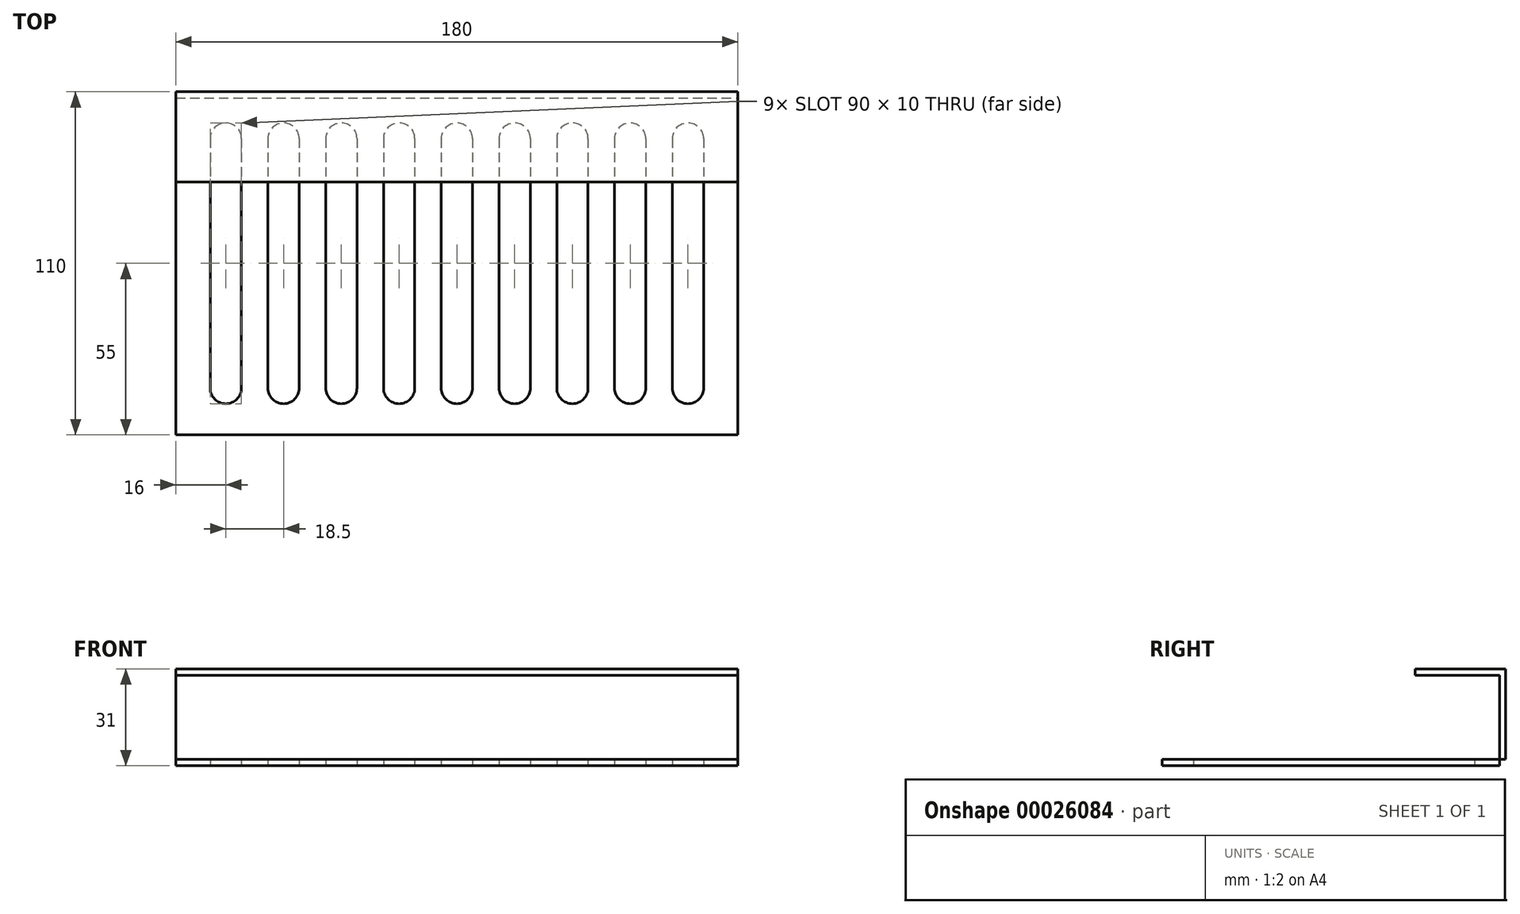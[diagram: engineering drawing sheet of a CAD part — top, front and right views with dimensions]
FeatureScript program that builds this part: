
annotation { "Feature Type Name" : "Feature", "Feature Type Description" : "" }
export const myFeature = defineFeature(function(context is Context, id is Id, definition is map)
    precondition{}
    {
        {
            var Q0;
            Q0=qCreatedBy(makeId("Top.planeOp"),FACE);
            var sketch = newSketch(context, id + "F0", { "sketchPlane" : qUnion([Q0])});
            skLineSegment(sketch, "E0.bottom", {"start": v(0, 0) * mm, "end": v(180, 0) * mm});
            skLineSegment(sketch, "E0.top", {"start": v(0, -108) * mm, "end": v(180, -108) * mm});
            skLineSegment(sketch, "E0.left", {"start": v(0, 0) * mm, "end": v(0, -108) * mm});
            skLineSegment(sketch, "E0.right", {"start": v(180, 0) * mm, "end": v(180, -108) * mm});
            skSolve(sketch);
        }
        {
            var Q0;
            Q0=makeQuery(id+"F0.imprint","IMPRINT",FACE,{"disambiguationData":[TD([[makeQuery(id+"F0.imprint","IMPRINT",EDGE,{"derivedFrom":sQuery(id+"F0.wireOp",EDGE,"E0.bottom")}),-1.0]])]});
            extrude(context, id + "F1", {"entities" : qUnion([Q0]), "depth" : 2 * mm});
        }
        {
            var Q0;
            Q0=makeQuery(id+"F1.opExtrude","SWEPT_FACE",FACE,{"disambiguationData":[OSD([sQuery(id+"F0.wireOp",EDGE,"E0.bottom")])]});
            var sketch = newSketch(context, id + "F2", { "sketchPlane" : qUnion([Q0])});
            skLineSegment(sketch, "E1.0", {"start": v(0, 0) * mm, "end": v(-180, 0) * mm});
            skLineSegment(sketch, "E2.0", {"start": v(-180, 2) * mm, "end": v(-180, 0) * mm});
            skLineSegment(sketch, "E3.0", {"start": v(0, 2) * mm, "end": v(0, 0) * mm});
            skLineSegment(sketch, "E4.bottom", {"start": v(-180, 0) * mm, "end": v(0, 0) * mm});
            skLineSegment(sketch, "E4.top", {"start": v(-180, 29) * mm, "end": v(0, 29) * mm});
            skLineSegment(sketch, "E4.left", {"start": v(-180, 0) * mm, "end": v(-180, 29) * mm});
            skLineSegment(sketch, "E4.right", {"start": v(0, 0) * mm, "end": v(0, 29) * mm});
            skSolve(sketch);
        }
        {
            var Q0;
            {var subQ1=sQuery(id+"F2.wireOp",EDGE,"E4.top");Q0=makeQuery(id+"F2.imprint","IMPRINT",FACE,{"disambiguationData":[TD([[makeQuery(id+"F2.imprint","IMPRINT",EDGE,{"derivedFrom":subQ1}),-1.0]])]});}
            var Q1;
            {var subQ2=sQuery(id+"F2.wireOp",EDGE,"E4.bottom");Q1=makeQuery(id+"F2.imprint","IMPRINT",FACE,{"disambiguationData":[TD([[makeQuery(id+"F2.imprint","IMPRINT",EDGE,{"derivedFrom":subQ2}),-1.0]])]});}
            extrude(context, id + "F3", {"entities" : qUnion([Q0, Q1]), "operationType" : NewBodyOperationType.ADD, "depth" : 2 * mm});
        }
        {
            var Q0;
            Q0=makeQuery(id+"F3.opExtrude","SWEPT_FACE",FACE,{"disambiguationData":[OSD([sQuery(id+"F2.wireOp",EDGE,"E4.top")])]});
            var sketch = newSketch(context, id + "F4", { "sketchPlane" : qUnion([Q0])});
            skLineSegment(sketch, "E5.0", {"start": v(180, 2) * mm, "end": v(180, 0) * mm});
            skLineSegment(sketch, "E6.0", {"start": v(180, 2) * mm, "end": v(0, 2) * mm});
            skLineSegment(sketch, "E7.0", {"start": v(0, 2) * mm, "end": v(0, 0) * mm});
            skLineSegment(sketch, "E8.left", {"start": v(180, 2) * mm, "end": v(180, 2) * mm});
            skLineSegment(sketch, "E8.right", {"start": v(0, 2) * mm, "end": v(0, 2) * mm});
            skLineSegment(sketch, "E9.top", {"start": v(180, -27) * mm, "end": v(0, -27) * mm});
            skLineSegment(sketch, "E9.left", {"start": v(180, 2) * mm, "end": v(180, -27) * mm});
            skLineSegment(sketch, "E9.right", {"start": v(0, 2) * mm, "end": v(0, -27) * mm});
            skSolve(sketch);
        }
        {
            var Q0;
            {var subQ2=sQuery(id+"F4.wireOp",EDGE,"E9.top");Q0=makeQuery(id+"F4.imprint","IMPRINT",FACE,{"disambiguationData":[TD([[makeQuery(id+"F4.imprint","IMPRINT",EDGE,{"derivedFrom":subQ2}),-1.0]])]});}
            var Q1;
            {var subQ2=sQuery(id+"F4.wireOp",EDGE,"E6.0");Q1=makeQuery(id+"F4.imprint","IMPRINT",FACE,{"disambiguationData":[TD([[makeQuery(id+"F4.imprint","IMPRINT",EDGE,{"derivedFrom":subQ2}),1.0]])]});}
            extrude(context, id + "F5", {"entities" : qUnion([Q0, Q1]), "operationType" : NewBodyOperationType.ADD, "depth" : 2 * mm});
        }
        {
            var Q0;
            Q0=makeQuery(id+"F3.boolean.opBoolean","MERGE",FACE,{"derivedFrom":[makeQuery(id+"F1.opExtrude","CAP_FACE",FACE,{"disambiguationData":[OSD([sQuery(id+"F0.wireOp",EDGE,"E0.bottom"),sQuery(id+"F0.wireOp",EDGE,"E0.top"),sQuery(id+"F0.wireOp",EDGE,"E0.left"),sQuery(id+"F0.wireOp",EDGE,"E0.right")])],"isStart":true}),makeQuery(id+"F3.opExtrude","SWEPT_FACE",FACE,{"disambiguationData":[OSD([sQuery(id+"F2.wireOp",EDGE,"E4.bottom")])]})]});
            var sketch = newSketch(context, id + "F6", { "sketchPlane" : qUnion([Q0])});
            skLineSegment(sketch, "E10.0", {"start": v(180, -2) * mm, "end": v(180, 108) * mm});
            skLineSegment(sketch, "E11.0", {"start": v(0, -2) * mm, "end": v(180, -2) * mm});
            skLineSegment(sketch, "E12.0", {"start": v(0, -2) * mm, "end": v(0, 108) * mm});
            skLineSegment(sketch, "E13.0", {"start": v(0, 108) * mm, "end": v(180, 108) * mm});
            skLineSegment(sketch, "E14.0", {"start": v(0, 8) * mm, "end": v(180, 8) * mm, "construction": true});
            skLineSegment(sketch, "E15.0", {"start": v(10, -2) * mm, "end": v(10, 110) * mm, "construction": true});
            skLineSegment(sketch, "E16.0", {"start": v(0, 98) * mm, "end": v(180, 98) * mm, "construction": true});
            skLineSegment(sketch, "E17.0", {"start": v(170, -2) * mm, "end": v(170, 110) * mm, "construction": true});
            skLineSegment(sketch, "E18", {"start": v(90, 8) * mm, "end": v(90, 98) * mm, "construction": true});
            skLineSegment(sketch, "E19.0", {"start": v(95, 13) * mm, "end": v(95, 93) * mm});
            skLineSegment(sketch, "E20.0", {"start": v(85, 13) * mm, "end": v(85, 93) * mm});
            skLineSegment(sketch, "E21", {"start": v(90, 8) * mm, "end": v(90, 8) * mm});
            skLineSegment(sketch, "E22", {"start": v(90, 98) * mm, "end": v(90, 98) * mm});
            skPoint(sketch, "E23.visualSharp", {"position": v(85, 8) * mm});
            skArc(sketch, "E23.filletArc", {"start": v(85, 13) * mm, "mid": v(86.46, 9.46) * mm, "end": v(90, 8) * mm});
            skPoint(sketch, "E24.visualSharp", {"position": v(95, 8) * mm});
            skArc(sketch, "E24.filletArc", {"start": v(90, 8) * mm, "mid": v(93.54, 9.46) * mm, "end": v(95, 13) * mm});
            skPoint(sketch, "E25.visualSharp", {"position": v(95, 98) * mm});
            skArc(sketch, "E25.filletArc", {"start": v(95, 93) * mm, "mid": v(93.54, 96.54) * mm, "end": v(90, 98) * mm});
            skPoint(sketch, "E26.visualSharp", {"position": v(85, 98) * mm});
            skArc(sketch, "E26.filletArc", {"start": v(90, 98) * mm, "mid": v(86.46, 96.54) * mm, "end": v(85, 93) * mm});
            skLineSegment(sketch, "E27.1.0.0", {"start": v(113.5, 13) * mm, "end": v(113.5, 93) * mm});
            skArc(sketch, "E27.1.0.1", {"start": v(108.5, 8) * mm, "mid": v(112.04, 9.46) * mm, "end": v(113.5, 13) * mm});
            skLineSegment(sketch, "E27.1.0.2", {"start": v(108.5, 8) * mm, "end": v(108.5, 8) * mm});
            skArc(sketch, "E27.1.0.3", {"start": v(103.5, 13) * mm, "mid": v(104.96, 9.46) * mm, "end": v(108.5, 8) * mm});
            skLineSegment(sketch, "E27.1.0.4", {"start": v(103.5, 13) * mm, "end": v(103.5, 93) * mm});
            skArc(sketch, "E27.1.0.5", {"start": v(113.5, 93) * mm, "mid": v(112.04, 96.54) * mm, "end": v(108.5, 98) * mm});
            skArc(sketch, "E27.1.0.6", {"start": v(108.5, 98) * mm, "mid": v(104.96, 96.54) * mm, "end": v(103.5, 93) * mm});
            skLineSegment(sketch, "E27.1.0.7", {"start": v(108.5, 98) * mm, "end": v(108.5, 98) * mm});
            skLineSegment(sketch, "E27.2.0.0", {"start": v(132, 13) * mm, "end": v(132, 93) * mm});
            skArc(sketch, "E27.2.0.1", {"start": v(127, 8) * mm, "mid": v(130.54, 9.46) * mm, "end": v(132, 13) * mm});
            skLineSegment(sketch, "E27.2.0.2", {"start": v(127, 8) * mm, "end": v(127, 8) * mm});
            skArc(sketch, "E27.2.0.3", {"start": v(122, 13) * mm, "mid": v(123.46, 9.46) * mm, "end": v(127, 8) * mm});
            skLineSegment(sketch, "E27.2.0.4", {"start": v(122, 13) * mm, "end": v(122, 93) * mm});
            skArc(sketch, "E27.2.0.5", {"start": v(132, 93) * mm, "mid": v(130.54, 96.54) * mm, "end": v(127, 98) * mm});
            skArc(sketch, "E27.2.0.6", {"start": v(127, 98) * mm, "mid": v(123.46, 96.54) * mm, "end": v(122, 93) * mm});
            skLineSegment(sketch, "E27.2.0.7", {"start": v(127, 98) * mm, "end": v(127, 98) * mm});
            skLineSegment(sketch, "E27.3.0.0", {"start": v(150.5, 13) * mm, "end": v(150.5, 93) * mm});
            skArc(sketch, "E27.3.0.1", {"start": v(145.5, 8) * mm, "mid": v(149.04, 9.46) * mm, "end": v(150.5, 13) * mm});
            skLineSegment(sketch, "E27.3.0.2", {"start": v(145.5, 8) * mm, "end": v(145.5, 8) * mm});
            skArc(sketch, "E27.3.0.3", {"start": v(140.5, 13) * mm, "mid": v(141.96, 9.46) * mm, "end": v(145.5, 8) * mm});
            skLineSegment(sketch, "E27.3.0.4", {"start": v(140.5, 13) * mm, "end": v(140.5, 93) * mm});
            skArc(sketch, "E27.3.0.5", {"start": v(150.5, 93) * mm, "mid": v(149.04, 96.54) * mm, "end": v(145.5, 98) * mm});
            skArc(sketch, "E27.3.0.6", {"start": v(145.5, 98) * mm, "mid": v(141.96, 96.54) * mm, "end": v(140.5, 93) * mm});
            skLineSegment(sketch, "E27.3.0.7", {"start": v(145.5, 98) * mm, "end": v(145.5, 98) * mm});
            skLineSegment(sketch, "E27.direction1", {"start": v(95, 13) * mm, "end": v(113.5, 13) * mm, "construction": true});
            skLineSegment(sketch, "E28.1.0.0", {"start": v(76.5, 13) * mm, "end": v(76.5, 93) * mm});
            skArc(sketch, "E28.1.0.1", {"start": v(71.5, 8) * mm, "mid": v(75.04, 9.46) * mm, "end": v(76.5, 13) * mm});
            skArc(sketch, "E28.1.0.2", {"start": v(66.5, 13) * mm, "mid": v(67.96, 9.46) * mm, "end": v(71.5, 8) * mm});
            skLineSegment(sketch, "E28.1.0.3", {"start": v(71.5, 8) * mm, "end": v(71.5, 8) * mm});
            skLineSegment(sketch, "E28.1.0.4", {"start": v(66.5, 13) * mm, "end": v(66.5, 93) * mm});
            skArc(sketch, "E28.1.0.5", {"start": v(76.5, 93) * mm, "mid": v(75.04, 96.54) * mm, "end": v(71.5, 98) * mm});
            skLineSegment(sketch, "E28.1.0.6", {"start": v(71.5, 98) * mm, "end": v(71.5, 98) * mm});
            skArc(sketch, "E28.1.0.7", {"start": v(71.5, 98) * mm, "mid": v(67.96, 96.54) * mm, "end": v(66.5, 93) * mm});
            skLineSegment(sketch, "E28.2.0.0", {"start": v(58, 13) * mm, "end": v(58, 93) * mm});
            skArc(sketch, "E28.2.0.1", {"start": v(53, 8) * mm, "mid": v(56.54, 9.46) * mm, "end": v(58, 13) * mm});
            skArc(sketch, "E28.2.0.2", {"start": v(48, 13) * mm, "mid": v(49.46, 9.46) * mm, "end": v(53, 8) * mm});
            skLineSegment(sketch, "E28.2.0.3", {"start": v(53, 8) * mm, "end": v(53, 8) * mm});
            skLineSegment(sketch, "E28.2.0.4", {"start": v(48, 13) * mm, "end": v(48, 93) * mm});
            skArc(sketch, "E28.2.0.5", {"start": v(58, 93) * mm, "mid": v(56.54, 96.54) * mm, "end": v(53, 98) * mm});
            skLineSegment(sketch, "E28.2.0.6", {"start": v(53, 98) * mm, "end": v(53, 98) * mm});
            skArc(sketch, "E28.2.0.7", {"start": v(53, 98) * mm, "mid": v(49.46, 96.54) * mm, "end": v(48, 93) * mm});
            skLineSegment(sketch, "E28.3.0.0", {"start": v(39.5, 13) * mm, "end": v(39.5, 93) * mm});
            skArc(sketch, "E28.3.0.1", {"start": v(34.5, 8) * mm, "mid": v(38.04, 9.46) * mm, "end": v(39.5, 13) * mm});
            skArc(sketch, "E28.3.0.2", {"start": v(29.5, 13) * mm, "mid": v(30.96, 9.46) * mm, "end": v(34.5, 8) * mm});
            skLineSegment(sketch, "E28.3.0.3", {"start": v(34.5, 8) * mm, "end": v(34.5, 8) * mm});
            skLineSegment(sketch, "E28.3.0.4", {"start": v(29.5, 13) * mm, "end": v(29.5, 93) * mm});
            skArc(sketch, "E28.3.0.5", {"start": v(39.5, 93) * mm, "mid": v(38.04, 96.54) * mm, "end": v(34.5, 98) * mm});
            skLineSegment(sketch, "E28.3.0.6", {"start": v(34.5, 98) * mm, "end": v(34.5, 98) * mm});
            skArc(sketch, "E28.3.0.7", {"start": v(34.5, 98) * mm, "mid": v(30.96, 96.54) * mm, "end": v(29.5, 93) * mm});
            skLineSegment(sketch, "E28.direction1", {"start": v(95, 13) * mm, "end": v(76.5, 13) * mm, "construction": true});
            skLineSegment(sketch, "E29.0.4.0", {"start": v(169, 13) * mm, "end": v(169, 93) * mm});
            skArc(sketch, "E29.3.4.0", {"start": v(164, 8) * mm, "mid": v(167.54, 9.46) * mm, "end": v(169, 13) * mm});
            skLineSegment(sketch, "E29.7.4.0", {"start": v(164, 8) * mm, "end": v(164, 8) * mm});
            skArc(sketch, "E29.10.4.0", {"start": v(159, 13) * mm, "mid": v(160.46, 9.46) * mm, "end": v(164, 8) * mm});
            skLineSegment(sketch, "E29.14.4.0", {"start": v(159, 13) * mm, "end": v(159, 93) * mm});
            skArc(sketch, "E29.17.4.0", {"start": v(169, 93) * mm, "mid": v(167.54, 96.54) * mm, "end": v(164, 98) * mm});
            skArc(sketch, "E29.21.4.0", {"start": v(164, 98) * mm, "mid": v(160.46, 96.54) * mm, "end": v(159, 93) * mm});
            skLineSegment(sketch, "E29.25.4.0", {"start": v(164, 98) * mm, "end": v(164, 98) * mm});
            skLineSegment(sketch, "E30.0.4.0", {"start": v(21, 13) * mm, "end": v(21, 93) * mm});
            skArc(sketch, "E30.3.4.0", {"start": v(16, 8) * mm, "mid": v(19.54, 9.46) * mm, "end": v(21, 13) * mm});
            skArc(sketch, "E30.7.4.0", {"start": v(11, 13) * mm, "mid": v(12.46, 9.46) * mm, "end": v(16, 8) * mm});
            skLineSegment(sketch, "E30.11.4.0", {"start": v(16, 8) * mm, "end": v(16, 8) * mm});
            skLineSegment(sketch, "E30.14.4.0", {"start": v(11, 13) * mm, "end": v(11, 93) * mm});
            skArc(sketch, "E30.17.4.0", {"start": v(21, 93) * mm, "mid": v(19.54, 96.54) * mm, "end": v(16, 98) * mm});
            skLineSegment(sketch, "E30.21.4.0", {"start": v(16, 98) * mm, "end": v(16, 98) * mm});
            skArc(sketch, "E30.24.4.0", {"start": v(16, 98) * mm, "mid": v(12.46, 96.54) * mm, "end": v(11, 93) * mm});
            skSolve(sketch);
        }
        {
            var Q0;
            Q0=makeQuery(id+"F6.imprint","IMPRINT",FACE,{"disambiguationData":[TD([[makeQuery(id+"F6.imprint","IMPRINT",EDGE,{"derivedFrom":sQuery(id+"F6.wireOp",EDGE,"E27.3.0.0")}),1.0]])]});
            var Q1;
            Q1=makeQuery(id+"F6.imprint","IMPRINT",FACE,{"disambiguationData":[TD([[makeQuery(id+"F6.imprint","IMPRINT",EDGE,{"derivedFrom":sQuery(id+"F6.wireOp",EDGE,"E27.2.0.0")}),1.0]])]});
            var Q2;
            Q2=makeQuery(id+"F6.imprint","IMPRINT",FACE,{"disambiguationData":[TD([[makeQuery(id+"F6.imprint","IMPRINT",EDGE,{"derivedFrom":sQuery(id+"F6.wireOp",EDGE,"E27.1.0.0")}),1.0]])]});
            var Q3;
            Q3=makeQuery(id+"F6.imprint","IMPRINT",FACE,{"disambiguationData":[TD([[makeQuery(id+"F6.imprint","IMPRINT",EDGE,{"derivedFrom":sQuery(id+"F6.wireOp",EDGE,"E19.0")}),1.0]])]});
            var Q4;
            Q4=makeQuery(id+"F6.imprint","IMPRINT",FACE,{"disambiguationData":[TD([[makeQuery(id+"F6.imprint","IMPRINT",EDGE,{"derivedFrom":sQuery(id+"F6.wireOp",EDGE,"E28.1.0.0")}),1.0]])]});
            var Q5;
            Q5=makeQuery(id+"F6.imprint","IMPRINT",FACE,{"disambiguationData":[TD([[makeQuery(id+"F6.imprint","IMPRINT",EDGE,{"derivedFrom":sQuery(id+"F6.wireOp",EDGE,"E28.2.0.0")}),1.0]])]});
            var Q6;
            Q6=makeQuery(id+"F6.imprint","IMPRINT",FACE,{"disambiguationData":[TD([[makeQuery(id+"F6.imprint","IMPRINT",EDGE,{"derivedFrom":sQuery(id+"F6.wireOp",EDGE,"E28.3.0.0")}),1.0]])]});
            var Q7;
            Q7=makeQuery(id+"F6.imprint","IMPRINT",FACE,{"disambiguationData":[TD([[makeQuery(id+"F6.imprint","IMPRINT",EDGE,{"derivedFrom":sQuery(id+"F6.wireOp",EDGE,"E29.0.4.0")}),1.0]])]});
            var Q8;
            Q8=makeQuery(id+"F6.imprint","IMPRINT",FACE,{"disambiguationData":[TD([[makeQuery(id+"F6.imprint","IMPRINT",EDGE,{"derivedFrom":sQuery(id+"F6.wireOp",EDGE,"E30.0.4.0")}),1.0]])]});
            extrude(context, id + "F7", {"entities" : qUnion([Q0, Q1, Q2, Q3, Q4, Q5, Q6, Q7, Q8]), "operationType" : NewBodyOperationType.REMOVE, "endBound" : BoundingType.UP_TO_NEXT, "oppositeDirection" : true, "depth" : 1.2 * mm});
        }
    });
